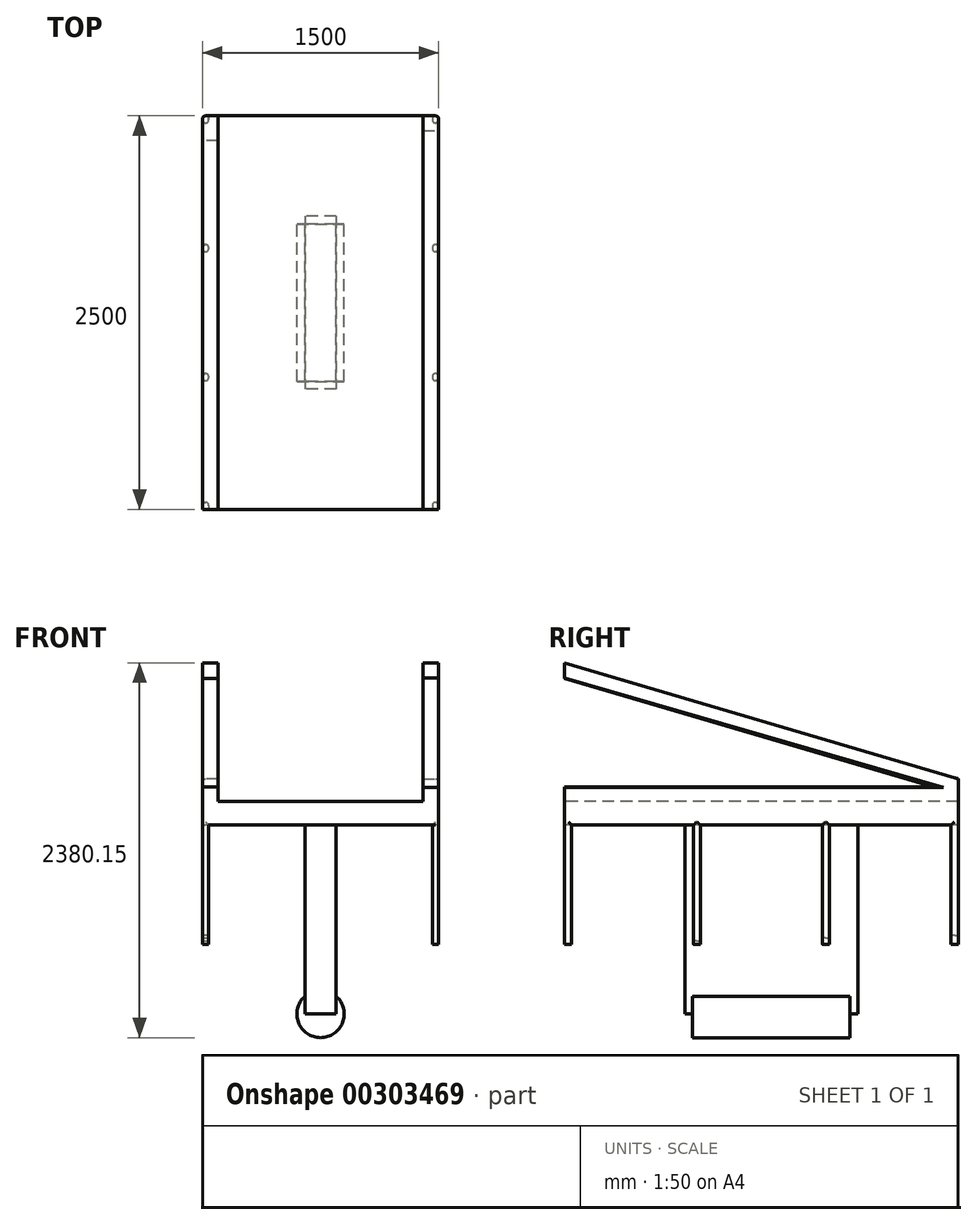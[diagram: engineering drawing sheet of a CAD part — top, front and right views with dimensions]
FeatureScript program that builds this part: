
annotation { "Feature Type Name" : "Feature", "Feature Type Description" : "" }
export const myFeature = defineFeature(function(context is Context, id is Id, definition is map)
    precondition{}
    {
        {
            var Q0;
            Q0=qCreatedBy(makeId("Front.planeOp"),FACE);
            var sketch = newSketch(context, id + "F0", { "sketchPlane" : qUnion([Q0])});
            skCircle(sketch, "E0", {"center": v(0, 0) * mm, "radius": 150 * mm});
            skSolve(sketch);
        }
        {
            var Q0;
            Q0=makeQuery(id+"F0.imprint","IMPRINT",FACE,{"disambiguationData":[TD([[makeQuery(id+"F0.imprint","IMPRINT",EDGE,{"derivedFrom":sQuery(id+"F0.wireOp",EDGE,"E0")}),1.0]])]});
            extrude(context, id + "F1", {"entities" : qUnion([Q0]), "depth" : 1000 * mm});
        }
        {
            var Q0;
            Q0=qCreatedBy(makeId("Top.planeOp"),FACE);
            var sketch = newSketch(context, id + "F2", { "sketchPlane" : qUnion([Q0])});
            skLineSegment(sketch, "E1.bottom", {"start": v(100, 50) * mm, "end": v(-100, 50) * mm});
            skLineSegment(sketch, "E1.top", {"start": v(100, -1050) * mm, "end": v(-100, -1050) * mm});
            skLineSegment(sketch, "E1.left", {"start": v(100, 50) * mm, "end": v(100, -1050) * mm});
            skLineSegment(sketch, "E1.right", {"start": v(-100, 50) * mm, "end": v(-100, -1050) * mm});
            skSolve(sketch);
        }
        {
            var Q0;
            Q0=makeQuery(id+"F2.imprint","IMPRINT",FACE,{"disambiguationData":[TD([[makeQuery(id+"F2.imprint","IMPRINT",EDGE,{"derivedFrom":sQuery(id+"F2.wireOp",EDGE,"E1.bottom")}),1.0]])]});
            extrude(context, id + "F3", {"entities" : qUnion([Q0]), "operationType" : NewBodyOperationType.ADD, "depth" : 1200 * mm});
        }
        {
            var Q0;
            Q0=makeQuery(id+"F3.opExtrude","CAP_FACE",FACE,{"disambiguationData":[OSD([sQuery(id+"F2.wireOp",EDGE,"E1.bottom"),sQuery(id+"F2.wireOp",EDGE,"E1.top"),sQuery(id+"F2.wireOp",EDGE,"E1.left"),sQuery(id+"F2.wireOp",EDGE,"E1.right")])],"isStart":false});
            var sketch = newSketch(context, id + "F4", { "sketchPlane" : qUnion([Q0])});
            skLineSegment(sketch, "E2.bottom", {"start": v(750, 686.42) * mm, "end": v(-750, 686.42) * mm});
            skLineSegment(sketch, "E2.top", {"start": v(750, -1813.58) * mm, "end": v(-750, -1813.58) * mm});
            skLineSegment(sketch, "E2.left", {"start": v(750, 686.42) * mm, "end": v(750, -1813.58) * mm});
            skLineSegment(sketch, "E2.right", {"start": v(-750, 686.42) * mm, "end": v(-750, -1813.58) * mm});
            skSolve(sketch);
        }
        {
            var Q0;
            Q0=makeQuery(id+"F4.imprint","IMPRINT",FACE,{"disambiguationData":[TD([[makeQuery(id+"F4.imprint","IMPRINT",EDGE,{"derivedFrom":sQuery(id+"F4.wireOp",EDGE,"E2.bottom")}),1.0]])]});
            var Q1;
            Q1=makeQuery(id+"F4.imprint","IMPRINT",FACE,{"disambiguationData":[TD([[makeQuery(id+"F4.imprint","IMPRINT",EDGE,{"derivedFrom":makeQuery(id+"F3.opExtrude","CAP_EDGE",EDGE,{"disambiguationData":[OSD([sQuery(id+"F2.wireOp",EDGE,"E1.bottom")])],"isStart":false})}),1.0]])]});
            extrude(context, id + "F5", {"entities" : qUnion([Q0, Q1]), "operationType" : NewBodyOperationType.ADD, "depth" : 150 * mm});
        }
        {
            var Q0;
            Q0=makeQuery(id+"F5.opExtrude","SWEPT_FACE",FACE,{"disambiguationData":[OSD([sQuery(id+"F4.wireOp",EDGE,"E2.left")])]});
            var sketch = newSketch(context, id + "F6", { "sketchPlane" : qUnion([Q0])});
            skLineSegment(sketch, "E3", {"start": v(686.42, 1350) * mm, "end": v(-1813.58, 1350) * mm});
            skLineSegment(sketch, "E4", {"start": v(-1813.58, 1350) * mm, "end": v(-1813.58, 1439.72) * mm});
            skLineSegment(sketch, "E5", {"start": v(-1813.58, 1439.72) * mm, "end": v(593.7, 1439.72) * mm});
            skLineSegment(sketch, "E6", {"start": v(593.7, 1439.72) * mm, "end": v(-1813.58, 2134.24) * mm});
            skLineSegment(sketch, "E7", {"start": v(-1813.58, 2134.24) * mm, "end": v(-1813.58, 2229.87) * mm});
            skLineSegment(sketch, "E8", {"start": v(-1813.58, 2229.87) * mm, "end": v(686.42, 1494.15) * mm});
            skLineSegment(sketch, "E9", {"start": v(686.42, 1494.15) * mm, "end": v(686.42, 1350) * mm});
            skSolve(sketch);
        }
        {
            var Q0;
            Q0=makeQuery(id+"F6.imprint","IMPRINT",FACE,{"disambiguationData":[TD([[makeQuery(id+"F6.imprint","IMPRINT",EDGE,{"derivedFrom":sQuery(id+"F6.wireOp",EDGE,"E3")}),-1.0]])]});
            extrude(context, id + "F7", {"entities" : qUnion([Q0]), "operationType" : NewBodyOperationType.ADD, "oppositeDirection" : true, "depth" : 100 * mm});
        }
        {
            var Q0;
            Q0=makeQuery(id+"F5.opExtrude","SWEPT_FACE",FACE,{"disambiguationData":[OSD([sQuery(id+"F4.wireOp",EDGE,"E2.right")])]});
            var sketch = newSketch(context, id + "F8", { "sketchPlane" : qUnion([Q0])});
            skLineSegment(sketch, "E10", {"start": v(1813.58, 1350) * mm, "end": v(-686.42, 1350) * mm});
            skLineSegment(sketch, "E11", {"start": v(-686.42, 1350) * mm, "end": v(-686.42, 1492.99) * mm});
            skLineSegment(sketch, "E12", {"start": v(-686.42, 1492.99) * mm, "end": v(1813.58, 2230.15) * mm});
            skLineSegment(sketch, "E13", {"start": v(1813.58, 2230.15) * mm, "end": v(1813.58, 2132.44) * mm});
            skLineSegment(sketch, "E14", {"start": v(1813.58, 2132.44) * mm, "end": v(-530.3, 1441.31) * mm});
            skLineSegment(sketch, "E15", {"start": v(-530.3, 1441.31) * mm, "end": v(1813.58, 1441.31) * mm});
            skLineSegment(sketch, "E16", {"start": v(1813.58, 1441.31) * mm, "end": v(1813.58, 1350) * mm});
            skSolve(sketch);
        }
        {
            var Q0;
            Q0=makeQuery(id+"F8.imprint","IMPRINT",FACE,{"disambiguationData":[TD([[makeQuery(id+"F8.imprint","IMPRINT",EDGE,{"derivedFrom":sQuery(id+"F8.wireOp",EDGE,"E10")}),1.0]])]});
            extrude(context, id + "F9", {"entities" : qUnion([Q0]), "oppositeDirection" : true, "depth" : 100 * mm});
        }
        {
            var Q0;
            Q0=makeQuery(id+"F1.opExtrude","SWEPT_BODY",BODY,{"disambiguationData":[OSD([sQuery(id+"F0.wireOp",EDGE,"E0")])]});
            var Q1;
            Q1=makeQuery(id+"F9.opExtrude","SWEPT_BODY",BODY,{"disambiguationData":[OSD([sQuery(id+"F8.wireOp",EDGE,"E10"),sQuery(id+"F8.wireOp",EDGE,"E11"),sQuery(id+"F8.wireOp",EDGE,"E12"),sQuery(id+"F8.wireOp",EDGE,"E13"),sQuery(id+"F8.wireOp",EDGE,"E14"),sQuery(id+"F8.wireOp",EDGE,"E15"),sQuery(id+"F8.wireOp",EDGE,"E16")])]});
            booleanBodies(context, id + "F10", {"operationType" : BooleanOperationType.UNION, "tools" : qUnion([Q0, Q1])});
        }
        {
            var Q0;
            Q0=makeQuery(id+"F10.opBoolean","MERGE",FACE,{"derivedFrom":[makeQuery(id+"F5.opExtrude","SWEPT_FACE",FACE,{"disambiguationData":[OSD([sQuery(id+"F4.wireOp",EDGE,"E2.right")])]}),makeQuery(id+"F9.opExtrude","CAP_FACE",FACE,{"disambiguationData":[OSD([sQuery(id+"F8.wireOp",EDGE,"E10"),sQuery(id+"F8.wireOp",EDGE,"E11"),sQuery(id+"F8.wireOp",EDGE,"E12"),sQuery(id+"F8.wireOp",EDGE,"E13"),sQuery(id+"F8.wireOp",EDGE,"E14"),sQuery(id+"F8.wireOp",EDGE,"E15"),sQuery(id+"F8.wireOp",EDGE,"E16")])],"isStart":true})]});
            var sketch = newSketch(context, id + "F11", { "sketchPlane" : qUnion([Q0])});
            skLineSegment(sketch, "E17", {"start": v(1813.58, 1200) * mm, "end": v(1813.58, 444.04) * mm});
            skLineSegment(sketch, "E18", {"start": v(1813.58, 444.04) * mm, "end": v(1768.58, 444.04) * mm});
            skLineSegment(sketch, "E19", {"start": v(1768.58, 444.04) * mm, "end": v(1768.58, 1200) * mm});
            skLineSegment(sketch, "E20", {"start": v(1768.58, 1200) * mm, "end": v(1813.58, 1200) * mm});
            skLineSegment(sketch, "E21", {"start": v(995.58, 1200) * mm, "end": v(995.58, 465.12) * mm});
            skLineSegment(sketch, "E22", {"start": v(995.58, 465.12) * mm, "end": v(950.58, 465.12) * mm});
            skLineSegment(sketch, "E23", {"start": v(950.58, 465.12) * mm, "end": v(950.58, 1200) * mm});
            skLineSegment(sketch, "E24", {"start": v(950.58, 1200) * mm, "end": v(995.58, 1200) * mm});
            skLineSegment(sketch, "E25", {"start": v(176.58, 1200) * mm, "end": v(176.58, 483.83) * mm});
            skLineSegment(sketch, "E26", {"start": v(176.58, 483.83) * mm, "end": v(131.58, 483.83) * mm});
            skLineSegment(sketch, "E27", {"start": v(131.58, 483.83) * mm, "end": v(131.58, 1200) * mm});
            skLineSegment(sketch, "E28", {"start": v(131.58, 1200) * mm, "end": v(176.58, 1200) * mm});
            skLineSegment(sketch, "E29", {"start": v(-686.42, 1200) * mm, "end": v(-686.42, 498.25) * mm});
            skLineSegment(sketch, "E30", {"start": v(-686.42, 498.25) * mm, "end": v(-641.42, 498.25) * mm});
            skLineSegment(sketch, "E31", {"start": v(-641.42, 498.25) * mm, "end": v(-641.42, 1200) * mm});
            skLineSegment(sketch, "E32", {"start": v(-641.42, 1200) * mm, "end": v(-686.42, 1200) * mm});
            skSolve(sketch);
        }
        {
            var Q0;
            Q0 = qSketchRegion(id + "F11", true);
            extrude(context, id + "F12", {"entities" : qUnion([Q0]), "operationType" : NewBodyOperationType.ADD, "oppositeDirection" : true, "depth" : 40 * mm});
        }
        {
            var Q0;
            Q0=makeQuery(id+"F12.opExtrude","CAP_EDGE",EDGE,{"disambiguationData":[OSD([sQuery(id+"F11.wireOp",EDGE,"E19")])],"isStart":true});
            var Q1;
            Q1=makeQuery(id+"F12.opExtrude","CAP_EDGE",EDGE,{"disambiguationData":[OSD([sQuery(id+"F11.wireOp",EDGE,"E19")])],"isStart":false});
            var Q2;
            Q2=makeQuery(id+"F12.opExtrude","CAP_EDGE",EDGE,{"disambiguationData":[OSD([sQuery(id+"F11.wireOp",EDGE,"E23")])],"isStart":true});
            var Q3;
            Q3=makeQuery(id+"F12.opExtrude","CAP_EDGE",EDGE,{"disambiguationData":[OSD([sQuery(id+"F11.wireOp",EDGE,"E23")])],"isStart":false});
            var Q4;
            Q4=makeQuery(id+"F12.opExtrude","CAP_EDGE",EDGE,{"disambiguationData":[OSD([sQuery(id+"F11.wireOp",EDGE,"E21")])],"isStart":true});
            var Q5;
            Q5=makeQuery(id+"F12.opExtrude","CAP_EDGE",EDGE,{"disambiguationData":[OSD([sQuery(id+"F11.wireOp",EDGE,"E21")])],"isStart":false});
            var Q6;
            Q6=makeQuery(id+"F12.opExtrude","CAP_EDGE",EDGE,{"disambiguationData":[OSD([sQuery(id+"F11.wireOp",EDGE,"E27")])],"isStart":true});
            var Q7;
            Q7=makeQuery(id+"F12.opExtrude","CAP_EDGE",EDGE,{"disambiguationData":[OSD([sQuery(id+"F11.wireOp",EDGE,"E25")])],"isStart":true});
            var Q8;
            Q8=makeQuery(id+"F12.opExtrude","CAP_EDGE",EDGE,{"disambiguationData":[OSD([sQuery(id+"F11.wireOp",EDGE,"E27")])],"isStart":false});
            var Q9;
            Q9=makeQuery(id+"F12.boolean.opBoolean","MERGE",EDGE,{"derivedFrom":[makeQuery(id+"F10.opBoolean","MERGE",EDGE,{"derivedFrom":[makeQuery(id+"F5.opExtrude","SWEPT_EDGE",EDGE,{"disambiguationData":[OSD([sQuery(id+"F4.wireOp",EDGE,"E2.bottom"),sQuery(id+"F4.wireOp",EDGE,"E2.right")])]}),makeQuery(id+"F9.opExtrude","CAP_EDGE",EDGE,{"disambiguationData":[OSD([sQuery(id+"F8.wireOp",EDGE,"E11")])],"isStart":true})]}),makeQuery(id+"F12.opExtrude","CAP_EDGE",EDGE,{"disambiguationData":[OSD([sQuery(id+"F11.wireOp",EDGE,"E29")])],"isStart":true})]});
            var Q10;
            Q10=makeQuery(id+"F12.opExtrude","CAP_EDGE",EDGE,{"disambiguationData":[OSD([sQuery(id+"F11.wireOp",EDGE,"E31")])],"isStart":true});
            var Q11;
            Q11=makeQuery(id+"F12.opExtrude","CAP_EDGE",EDGE,{"disambiguationData":[OSD([sQuery(id+"F11.wireOp",EDGE,"E29")])],"isStart":false});
            var Q12;
            Q12=makeQuery(id+"F12.opExtrude","CAP_EDGE",EDGE,{"disambiguationData":[OSD([sQuery(id+"F11.wireOp",EDGE,"E25")])],"isStart":false});
            var Q13;
            Q13=makeQuery(id+"F12.opExtrude","CAP_EDGE",EDGE,{"disambiguationData":[OSD([sQuery(id+"F11.wireOp",EDGE,"E31")])],"isStart":false});
            var Q14;
            {var subQ0=sQuery(id+"F11.wireOp",EDGE,"E19");var subQ1=sQuery(id+"F4.wireOp",EDGE,"E2.right");Q14=makeQuery(id+"F12.boolean.opBoolean","SPLIT",EDGE,{"disambiguationData":[TD([makeQuery(id+"F12.opExtrude","SWEPT_FACE",FACE,{"disambiguationData":[OSD([subQ0])]})])],"derivedFrom":makeQuery(id+"F5.opExtrude","CAP_EDGE",EDGE,{"disambiguationData":[OSD([subQ1])],"isStart":true})});}
            var Q15;
            {var subQ0=sQuery(id+"F4.wireOp",EDGE,"E2.right");var subQ2=sQuery(id+"F11.wireOp",EDGE,"E23");Q15=makeQuery(id+"F12.boolean.opBoolean","SPLIT",EDGE,{"disambiguationData":[TD([makeQuery(id+"F12.opExtrude","SWEPT_FACE",FACE,{"disambiguationData":[OSD([subQ2])]})])],"derivedFrom":makeQuery(id+"F5.opExtrude","CAP_EDGE",EDGE,{"disambiguationData":[OSD([subQ0])],"isStart":true})});}
            var Q16;
            {var subQ0=sQuery(id+"F4.wireOp",EDGE,"E2.right");var subQ2=sQuery(id+"F11.wireOp",EDGE,"E27");Q16=makeQuery(id+"F12.boolean.opBoolean","SPLIT",EDGE,{"disambiguationData":[TD([makeQuery(id+"F12.opExtrude","SWEPT_FACE",FACE,{"disambiguationData":[OSD([subQ2])]})])],"derivedFrom":makeQuery(id+"F5.opExtrude","CAP_EDGE",EDGE,{"disambiguationData":[OSD([subQ0])],"isStart":true})});}
            fillet(context, id + "F13", {"entities" : qUnion([Q0, Q1, Q2, Q3, Q4, Q5, Q6, Q7, Q8, Q9, Q10, Q11, Q12, Q13, Q14, Q15, Q16]), "radius" : 20 * mm, "tangentPropagation" : true, "allowEdgeOverflow" : false});
        }
        {
            var Q0;
            Q0=makeQuery(id+"F7.boolean.opBoolean","MERGE",FACE,{"derivedFrom":[makeQuery(id+"F5.opExtrude","SWEPT_FACE",FACE,{"disambiguationData":[OSD([sQuery(id+"F4.wireOp",EDGE,"E2.left")])]}),makeQuery(id+"F7.opExtrude","CAP_FACE",FACE,{"disambiguationData":[OSD([sQuery(id+"F6.wireOp",EDGE,"E3"),sQuery(id+"F6.wireOp",EDGE,"E4"),sQuery(id+"F6.wireOp",EDGE,"E5"),sQuery(id+"F6.wireOp",EDGE,"E6"),sQuery(id+"F6.wireOp",EDGE,"E7"),sQuery(id+"F6.wireOp",EDGE,"E8"),sQuery(id+"F6.wireOp",EDGE,"E9")])],"isStart":true})]});
            var sketch = newSketch(context, id + "F14", { "sketchPlane" : qUnion([Q0])});
            skLineSegment(sketch, "E33", {"start": v(-1813.58, 1200) * mm, "end": v(-1813.58, 444.04) * mm});
            skLineSegment(sketch, "E34", {"start": v(-1813.58, 444.04) * mm, "end": v(-1768.58, 444.04) * mm});
            skLineSegment(sketch, "E35", {"start": v(-1768.58, 444.04) * mm, "end": v(-1768.58, 1200) * mm});
            skLineSegment(sketch, "E36", {"start": v(-1768.58, 1200) * mm, "end": v(-1813.58, 1200) * mm});
            skLineSegment(sketch, "E37", {"start": v(-995.58, 1200) * mm, "end": v(-995.58, 444.04) * mm});
            skLineSegment(sketch, "E38", {"start": v(-995.58, 444.04) * mm, "end": v(-950.58, 444.04) * mm});
            skLineSegment(sketch, "E39", {"start": v(-950.58, 444.04) * mm, "end": v(-950.58, 1200) * mm});
            skLineSegment(sketch, "E40", {"start": v(-950.58, 1200) * mm, "end": v(-995.58, 1200) * mm});
            skLineSegment(sketch, "E41", {"start": v(-176.58, 1200) * mm, "end": v(-176.58, 444.04) * mm});
            skLineSegment(sketch, "E42", {"start": v(-176.58, 444.04) * mm, "end": v(-131.58, 444.04) * mm});
            skLineSegment(sketch, "E43", {"start": v(-131.58, 444.04) * mm, "end": v(-131.58, 1200) * mm});
            skLineSegment(sketch, "E44", {"start": v(-131.58, 1200) * mm, "end": v(-176.58, 1200) * mm});
            skLineSegment(sketch, "E45", {"start": v(686.42, 1200) * mm, "end": v(686.42, 444.04) * mm});
            skLineSegment(sketch, "E46", {"start": v(686.42, 444.04) * mm, "end": v(641.42, 444.04) * mm});
            skLineSegment(sketch, "E47", {"start": v(641.42, 444.04) * mm, "end": v(641.42, 1200) * mm});
            skLineSegment(sketch, "E48", {"start": v(641.42, 1200) * mm, "end": v(686.42, 1200) * mm});
            skSolve(sketch);
        }
        {
            var Q0;
            Q0 = qSketchRegion(id + "F14", true);
            extrude(context, id + "F15", {"entities" : qUnion([Q0]), "oppositeDirection" : true, "depth" : 40 * mm});
        }
        {
            var Q0;
            Q0=makeQuery(id+"F1.opExtrude","SWEPT_BODY",BODY,{"disambiguationData":[OSD([sQuery(id+"F0.wireOp",EDGE,"E0")])]});
            var Q1;
            Q1=makeQuery(id+"F15.opExtrude","SWEPT_BODY",BODY,{"disambiguationData":[OSD([sQuery(id+"F14.wireOp",EDGE,"E33"),sQuery(id+"F14.wireOp",EDGE,"E34"),sQuery(id+"F14.wireOp",EDGE,"E35"),sQuery(id+"F14.wireOp",EDGE,"E36")])]});
            var Q2;
            Q2=makeQuery(id+"F15.opExtrude","SWEPT_BODY",BODY,{"disambiguationData":[OSD([sQuery(id+"F14.wireOp",EDGE,"E37"),sQuery(id+"F14.wireOp",EDGE,"E38"),sQuery(id+"F14.wireOp",EDGE,"E39"),sQuery(id+"F14.wireOp",EDGE,"E40")])]});
            var Q3;
            Q3=makeQuery(id+"F15.opExtrude","SWEPT_BODY",BODY,{"disambiguationData":[OSD([sQuery(id+"F14.wireOp",EDGE,"E41"),sQuery(id+"F14.wireOp",EDGE,"E42"),sQuery(id+"F14.wireOp",EDGE,"E43"),sQuery(id+"F14.wireOp",EDGE,"E44")])]});
            var Q4;
            Q4=makeQuery(id+"F15.opExtrude","SWEPT_BODY",BODY,{"disambiguationData":[OSD([sQuery(id+"F14.wireOp",EDGE,"E45"),sQuery(id+"F14.wireOp",EDGE,"E46"),sQuery(id+"F14.wireOp",EDGE,"E47"),sQuery(id+"F14.wireOp",EDGE,"E48")])]});
            booleanBodies(context, id + "F16", {"operationType" : BooleanOperationType.UNION, "tools" : qUnion([Q0, Q1, Q2, Q3, Q4])});
        }
        {
            var Q0;
            Q0=makeQuery(id+"F16.opBoolean","MERGE",EDGE,{"derivedFrom":[makeQuery(id+"F7.boolean.opBoolean","MERGE",EDGE,{"derivedFrom":[makeQuery(id+"F5.opExtrude","SWEPT_EDGE",EDGE,{"disambiguationData":[OSD([sQuery(id+"F4.wireOp",EDGE,"E2.bottom"),sQuery(id+"F4.wireOp",EDGE,"E2.left")])]}),makeQuery(id+"F7.opExtrude","CAP_EDGE",EDGE,{"disambiguationData":[OSD([sQuery(id+"F6.wireOp",EDGE,"E9")])],"isStart":true})]}),makeQuery(id+"F15.opExtrude","CAP_EDGE",EDGE,{"disambiguationData":[OSD([sQuery(id+"F14.wireOp",EDGE,"E45")])],"isStart":true})]});
            var Q1;
            Q1=makeQuery(id+"F15.opExtrude","CAP_EDGE",EDGE,{"disambiguationData":[OSD([sQuery(id+"F14.wireOp",EDGE,"E45")])],"isStart":false});
            var Q2;
            Q2=makeQuery(id+"F15.opExtrude","CAP_EDGE",EDGE,{"disambiguationData":[OSD([sQuery(id+"F14.wireOp",EDGE,"E47")])],"isStart":true});
            var Q3;
            Q3=makeQuery(id+"F15.opExtrude","CAP_EDGE",EDGE,{"disambiguationData":[OSD([sQuery(id+"F14.wireOp",EDGE,"E43")])],"isStart":true});
            var Q4;
            Q4=makeQuery(id+"F15.opExtrude","CAP_EDGE",EDGE,{"disambiguationData":[OSD([sQuery(id+"F14.wireOp",EDGE,"E43")])],"isStart":false});
            var Q5;
            Q5=makeQuery(id+"F15.opExtrude","CAP_EDGE",EDGE,{"disambiguationData":[OSD([sQuery(id+"F14.wireOp",EDGE,"E41")])],"isStart":true});
            var Q6;
            Q6=makeQuery(id+"F15.opExtrude","CAP_EDGE",EDGE,{"disambiguationData":[OSD([sQuery(id+"F14.wireOp",EDGE,"E39")])],"isStart":true});
            var Q7;
            Q7=makeQuery(id+"F15.opExtrude","CAP_EDGE",EDGE,{"disambiguationData":[OSD([sQuery(id+"F14.wireOp",EDGE,"E39")])],"isStart":false});
            var Q8;
            Q8=makeQuery(id+"F15.opExtrude","CAP_EDGE",EDGE,{"disambiguationData":[OSD([sQuery(id+"F14.wireOp",EDGE,"E37")])],"isStart":true});
            var Q9;
            Q9=makeQuery(id+"F15.opExtrude","CAP_EDGE",EDGE,{"disambiguationData":[OSD([sQuery(id+"F14.wireOp",EDGE,"E35")])],"isStart":false});
            var Q10;
            Q10=makeQuery(id+"F15.opExtrude","CAP_EDGE",EDGE,{"disambiguationData":[OSD([sQuery(id+"F14.wireOp",EDGE,"E35")])],"isStart":true});
            var Q11;
            Q11=makeQuery(id+"F16.opBoolean","MERGE",EDGE,{"derivedFrom":[makeQuery(id+"F7.boolean.opBoolean","MERGE",EDGE,{"derivedFrom":[makeQuery(id+"F5.opExtrude","SWEPT_EDGE",EDGE,{"disambiguationData":[OSD([sQuery(id+"F4.wireOp",EDGE,"E2.top"),sQuery(id+"F4.wireOp",EDGE,"E2.left")])]}),makeQuery(id+"F7.opExtrude","CAP_EDGE",EDGE,{"disambiguationData":[OSD([sQuery(id+"F6.wireOp",EDGE,"E4")])],"isStart":true})]}),makeQuery(id+"F15.opExtrude","CAP_EDGE",EDGE,{"disambiguationData":[OSD([sQuery(id+"F14.wireOp",EDGE,"E33")])],"isStart":true})]});
            var Q12;
            Q12=makeQuery(id+"F15.opExtrude","CAP_EDGE",EDGE,{"disambiguationData":[OSD([sQuery(id+"F14.wireOp",EDGE,"E37")])],"isStart":false});
            var Q13;
            Q13=makeQuery(id+"F15.opExtrude","CAP_EDGE",EDGE,{"disambiguationData":[OSD([sQuery(id+"F14.wireOp",EDGE,"E33")])],"isStart":false});
            var Q14;
            Q14=makeQuery(id+"F15.opExtrude","CAP_EDGE",EDGE,{"disambiguationData":[OSD([sQuery(id+"F14.wireOp",EDGE,"E41")])],"isStart":false});
            var Q15;
            Q15=makeQuery(id+"F15.opExtrude","CAP_EDGE",EDGE,{"disambiguationData":[OSD([sQuery(id+"F14.wireOp",EDGE,"E47")])],"isStart":false});
            var Q16;
            {var subQ0=sQuery(id+"F4.wireOp",EDGE,"E2.left");var subQ1=sQuery(id+"F14.wireOp",EDGE,"E43");Q16=makeQuery(id+"F16.opBoolean","SPLIT",EDGE,{"disambiguationData":[TD([makeQuery(id+"F15.opExtrude","SWEPT_FACE",FACE,{"disambiguationData":[OSD([subQ1])]})])],"derivedFrom":makeQuery(id+"F5.opExtrude","CAP_EDGE",EDGE,{"disambiguationData":[OSD([subQ0])],"isStart":true})});}
            var Q17;
            {var subQ1=sQuery(id+"F4.wireOp",EDGE,"E2.left");var subQ2=sQuery(id+"F14.wireOp",EDGE,"E39");Q17=makeQuery(id+"F16.opBoolean","SPLIT",EDGE,{"disambiguationData":[TD([makeQuery(id+"F15.opExtrude","SWEPT_FACE",FACE,{"disambiguationData":[OSD([subQ2])]})])],"derivedFrom":makeQuery(id+"F5.opExtrude","CAP_EDGE",EDGE,{"disambiguationData":[OSD([subQ1])],"isStart":true})});}
            var Q18;
            {var subQ0=sQuery(id+"F14.wireOp",EDGE,"E35");var subQ1=sQuery(id+"F4.wireOp",EDGE,"E2.left");Q18=makeQuery(id+"F16.opBoolean","SPLIT",EDGE,{"disambiguationData":[TD([makeQuery(id+"F15.opExtrude","SWEPT_FACE",FACE,{"disambiguationData":[OSD([subQ0])]})])],"derivedFrom":makeQuery(id+"F5.opExtrude","CAP_EDGE",EDGE,{"disambiguationData":[OSD([subQ1])],"isStart":true})});}
            var Q19;
            Q19=makeQuery(id+"F5.opExtrude","CAP_EDGE",EDGE,{"disambiguationData":[OSD([sQuery(id+"F4.wireOp",EDGE,"E2.bottom")])],"isStart":true});
            fillet(context, id + "F17", {"entities" : qUnion([Q0, Q1, Q2, Q3, Q4, Q5, Q6, Q7, Q8, Q9, Q10, Q11, Q12, Q13, Q14, Q15, Q16, Q17, Q18, Q19]), "radius" : 20 * mm, "tangentPropagation" : true, "allowEdgeOverflow" : false});
        }
    });
